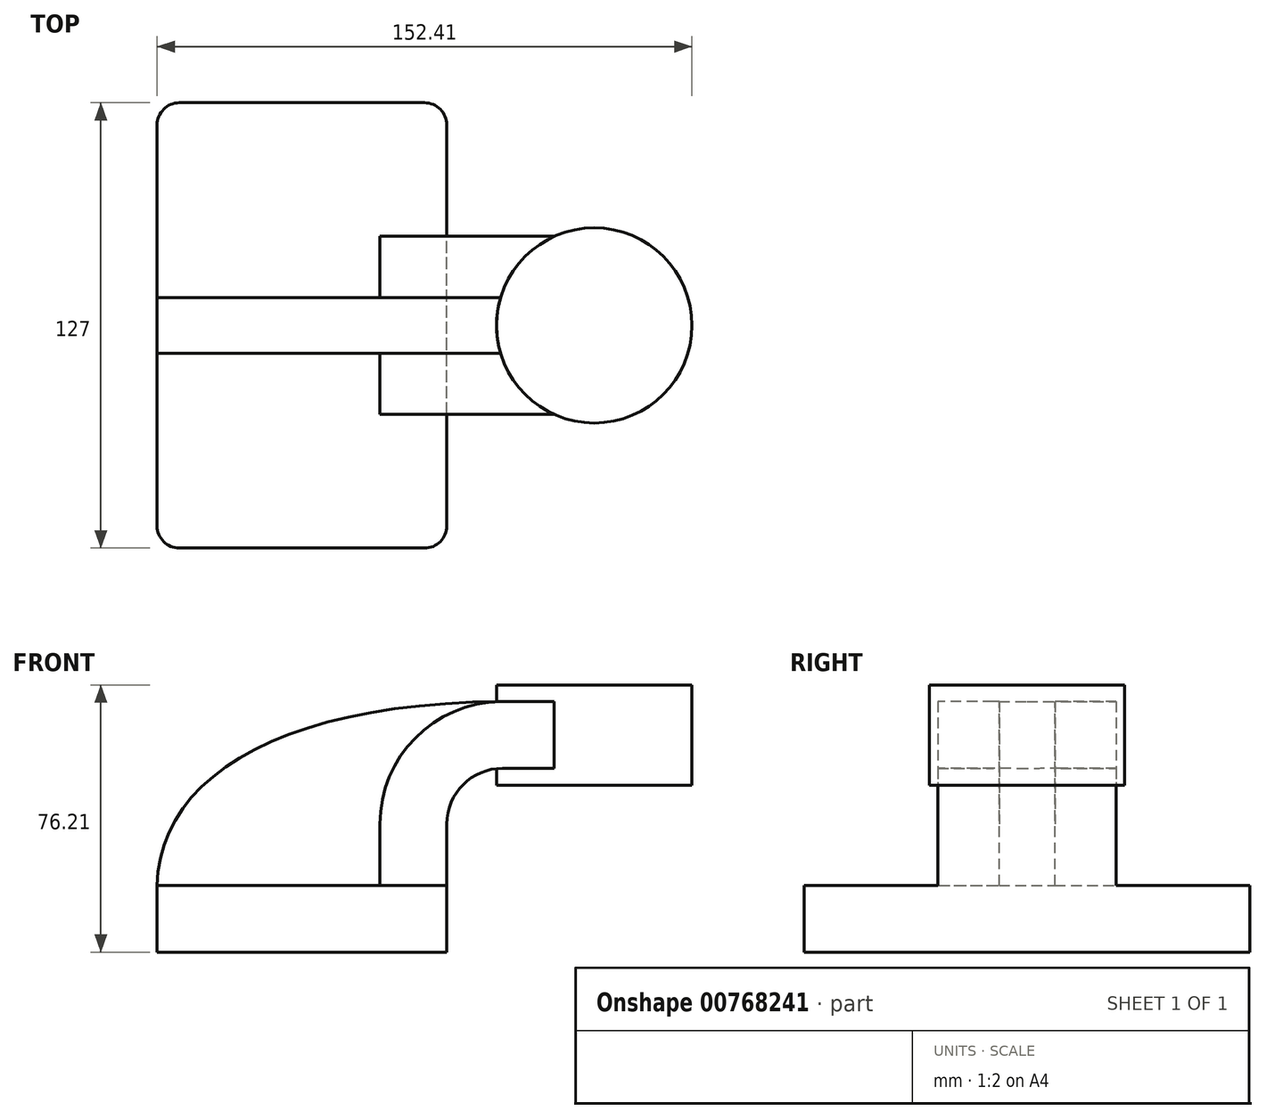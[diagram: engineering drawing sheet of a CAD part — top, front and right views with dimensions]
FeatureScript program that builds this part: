
annotation { "Feature Type Name" : "Feature", "Feature Type Description" : "" }
export const myFeature = defineFeature(function(context is Context, id is Id, definition is map)
    precondition{}
    {
        {
            var Q0;
            Q0=qCreatedBy(makeId("Front.planeOp"),FACE);
            var sketch = newSketch(context, id + "F0", { "sketchPlane" : qUnion([Q0])});
            skLineSegment(sketch, "E0.bottom", {"start": v(-41.28, -9.53) * mm, "end": v(41.28, -9.53) * mm});
            skLineSegment(sketch, "E0.top", {"start": v(-41.28, 9.53) * mm, "end": v(41.28, 9.53) * mm});
            skLineSegment(sketch, "E0.left", {"start": v(-41.28, -9.53) * mm, "end": v(-41.28, 9.53) * mm});
            skLineSegment(sketch, "E0.right", {"start": v(41.28, -9.53) * mm, "end": v(41.28, 9.53) * mm});
            skPoint(sketch, "E0.middle", {"position": v(0, 0) * mm});
            skLineSegment(sketch, "E1.bottom", {"start": v(111.12, 66.68) * mm, "end": v(60.32, 66.68) * mm});
            skLineSegment(sketch, "E1.top", {"start": v(111.12, 38.1) * mm, "end": v(60.32, 38.1) * mm});
            skLineSegment(sketch, "E1.left", {"start": v(111.12, 66.68) * mm, "end": v(111.12, 38.1) * mm});
            skLineSegment(sketch, "E1.right", {"start": v(60.32, 66.68) * mm, "end": v(60.32, 38.1) * mm});
            skPoint(sketch, "E1.middle", {"position": v(85.72, 52.39) * mm});
            skLineSegment(sketch, "E2", {"start": v(41.28, 9.52) * mm, "end": v(41.28, 27) * mm});
            skArc(sketch, "E3", {"start": v(41.27, 27) * mm, "mid": v(45.92, 38.23) * mm, "end": v(57.15, 42.88) * mm});
            skLineSegment(sketch, "E4", {"start": v(57.15, 42.88) * mm, "end": v(83.29, 42.88) * mm});
            skLineSegment(sketch, "E5.0", {"start": v(57.15, 208.61) * mm, "end": v(83.29, 208.61) * mm});
            skArc(sketch, "E5.1", {"start": v(-124.46, 27) * mm, "mid": v(-71.27, 155.42) * mm, "end": v(57.15, 208.61) * mm});
            skLineSegment(sketch, "E5.2", {"start": v(-124.46, 9.52) * mm, "end": v(-124.46, 27) * mm});
            skLineSegment(sketch, "E6.0", {"start": v(57.15, 61.93) * mm, "end": v(83.29, 61.93) * mm});
            skArc(sketch, "E6.1", {"start": v(22.22, 27) * mm, "mid": v(32.45, 51.7) * mm, "end": v(57.15, 61.93) * mm});
            skLineSegment(sketch, "E6.2", {"start": v(22.22, 9.52) * mm, "end": v(22.22, 27) * mm});
            skLineSegment(sketch, "E7", {"start": v(83.29, 38.1) * mm, "end": v(83.29, 66.68) * mm});
            skFitSpline(sketch, "E8", {"points": [v(-41.28, 9.53) * mm, v(57.15, 61.93) * mm], "startDerivative": vector(1.93, 92.26) * mm, "endDerivative": vector(189.84, 1.1) * mm});
            skSolve(sketch);
        }
        {
            var Q0;
            Q0=makeQuery(id+"F0.imprint","IMPRINT",FACE,{"disambiguationData":[TD([[makeQuery(id+"F0.imprint","IMPRINT",EDGE,{"derivedFrom":sQuery(id+"F0.wireOp",EDGE,"E0.bottom")}),1.0]])]});
            extrude(context, id + "F1", {"entities" : qUnion([Q0]), "depth" : 127 * mm, "offsetDistance" : 25.4 * mm, "symmetric" : true});
        }
        {
            var Q0;
            {var subQ1=sQuery(id+"F0.wireOp",EDGE,"E2");Q0=makeQuery(id+"F0.imprint","IMPRINT",FACE,{"disambiguationData":[TD([[makeQuery(id+"F0.imprint","IMPRINT",EDGE,{"derivedFrom":subQ1}),1.0]])]});}
            var Q1;
            {var subQ0=sQuery(id+"F0.wireOp",EDGE,"E6.0");var subQ1=sQuery(id+"F0.wireOp",EDGE,"E1.right");var subQ2=makeQuery(id+"F0.imprint","INTERSECT",VERTEX,{"derivedFrom":[subQ1,subQ0]});Q1=makeQuery(id+"F0.imprint","IMPRINT",FACE,{"disambiguationData":[TD([[makeQuery(id+"F0.imprint","IMPRINT",EDGE,{"disambiguationData":[TD([[subQ2,-1.0]])],"derivedFrom":subQ1}),1.0]])]});}
            extrude(context, id + "F2", {"entities" : qUnion([Q0, Q1]), "operationType" : NewBodyOperationType.ADD, "depth" : 50.8 * mm, "offsetDistance" : 25.4 * mm, "symmetric" : true});
        }
        {
            var Q0;
            {var subQ3=sQuery(id+"F0.wireOp",EDGE,"E6.2");Q0=makeQuery(id+"F0.imprint","IMPRINT",FACE,{"disambiguationData":[TD([[makeQuery(id+"F0.imprint","IMPRINT",EDGE,{"derivedFrom":subQ3}),1.0]])]});}
            extrude(context, id + "F3", {"entities" : qUnion([Q0]), "operationType" : NewBodyOperationType.ADD, "depth" : 15.88 * mm, "offsetDistance" : 25.4 * mm, "symmetric" : true});
        }
        {
            var Q0;
            {var subQ0=sQuery(id+"F0.wireOp",EDGE,"E1.left");Q0=makeQuery(id+"F0.imprint","IMPRINT",FACE,{"disambiguationData":[TD([[makeQuery(id+"F0.imprint","IMPRINT",EDGE,{"derivedFrom":subQ0}),-1.0]])]});}
            var Q1;
            Q1=sQuery(id+"F0.wireOp",EDGE,"E7");
            revolve(context, id + "F4", {"operationType" : NewBodyOperationType.ADD, "surfaceOperationType" : NewSurfaceOperationType.NEW, "entities" : qUnion([Q0]), "axis" : qUnion([Q1]), "revolveType" : RevolveType.FULL});
        }
        {
            var Q0;
            Q0=makeQuery(id+"F1.opExtrude","CAP_EDGE",EDGE,{"disambiguationData":[OSD([sQuery(id+"F0.wireOp",EDGE,"E0.right")])],"isStart":false});
            var Q1;
            Q1=makeQuery(id+"F1.opExtrude","CAP_EDGE",EDGE,{"disambiguationData":[OSD([sQuery(id+"F0.wireOp",EDGE,"E0.left")])],"isStart":false});
            var Q2;
            Q2=makeQuery(id+"F1.opExtrude","CAP_EDGE",EDGE,{"disambiguationData":[OSD([sQuery(id+"F0.wireOp",EDGE,"E0.left")])],"isStart":true});
            var Q3;
            Q3=makeQuery(id+"F1.opExtrude","CAP_EDGE",EDGE,{"disambiguationData":[OSD([sQuery(id+"F0.wireOp",EDGE,"E0.right")])],"isStart":true});
            fillet(context, id + "F5", {"entities" : qUnion([Q0, Q1, Q2, Q3]), "radius" : 6.35 * mm, "tangentPropagation" : true, "allowEdgeOverflow" : false});
        }
    });
